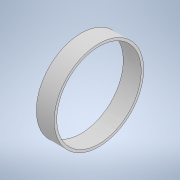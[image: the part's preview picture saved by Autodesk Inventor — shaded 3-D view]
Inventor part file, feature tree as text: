
AUTODESK INVENTOR PART (.ipt)
format: ipt  version: 2020 (Build 240168000, 168)  size: 102,912 bytes
history: native  units: mm
features: extrude x1, sketch x1
ambient origin geometry x8: Origin, YZ Plane, XZ Plane, XY Plane, X Axis, Y Axis, Z Axis, Center Point
bodies: Solid1 (feature_tree)
feature tree (2):
  extrude  "Extrusion1"  Depth=18.0mm
  sketch  "Sketch1"  dims[d0=85.0mm d1=2.5mm d2=18.0mm d3=0.0mm]
